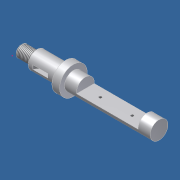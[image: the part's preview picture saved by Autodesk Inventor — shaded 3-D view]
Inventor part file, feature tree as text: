
AUTODESK INVENTOR PART (.ipt)
format: ipt  version: unknown  size: 237,568 bytes
history: native  units: in
note: dims shown in document units (in); Inventor stores cm internally (conversion verified against a paired STEP export)
features: sketch x5, plane x3, projected_geometry x3, extrude x2, revolve x1, hole x1, thread x1
ambient origin geometry x8: Origin, YZ Plane, XZ Plane, XY Plane, X Axis, Y Axis, Z Axis, Center Point
bodies: Solid1 (feature_tree)
feature tree (16):
  revolve  "Revolution1"  [1 undecoded]
  extrude  "Extrusion1"  Depth=4.325in
  hole  "Hole1"  [1 undecoded]
  thread  "Thread1"  [1 undecoded]
  plane  "Work Plane2"
  sketch  "Sketch4"  dims[d10=90.0deg d11=0.311in]
  plane  "Work Plane4"
  extrude  "Extrusion3"  Depth=0.311in
  sketch  "Sketch1"  dims[d2=0.436in d3=0.28in]
  sketch  "Sketch2"  dims[d4=0.24in d5=4.325in]
  projected_geometry  "Projected Loop1"
  projected_geometry  "Projected Loop2"
  projected_geometry  "Projected Loop3"
  sketch  "Sketch3"  dims[d6=0.1875in d7=0.28in d9=0.898in]
  plane  "Work Plane3"
  sketch  "Sketch6"  dims[d12=0.375in d13=1.937in d14=1.0in d15=0.0in d16=0.472in d17=1.0in d18=0.28in d19=0.089in d20=0.75in d21=0.375in d22=0.25in d23=0.5635in d24=1.0in d25=0.8108in d26=0.47in d27=0.0in d29=45.0deg d30=0.5in d31=0.03in d38=0.28in d39=0.375in d41=0.5in d42=0.125in d43=0.0in d44=0.56in d45=0.357in]
note: 3 required parameter values undecoded (feature->parameter linkage not recoverable at this tier; creation-order binding heuristic only, values carry confidence <= 0.55)